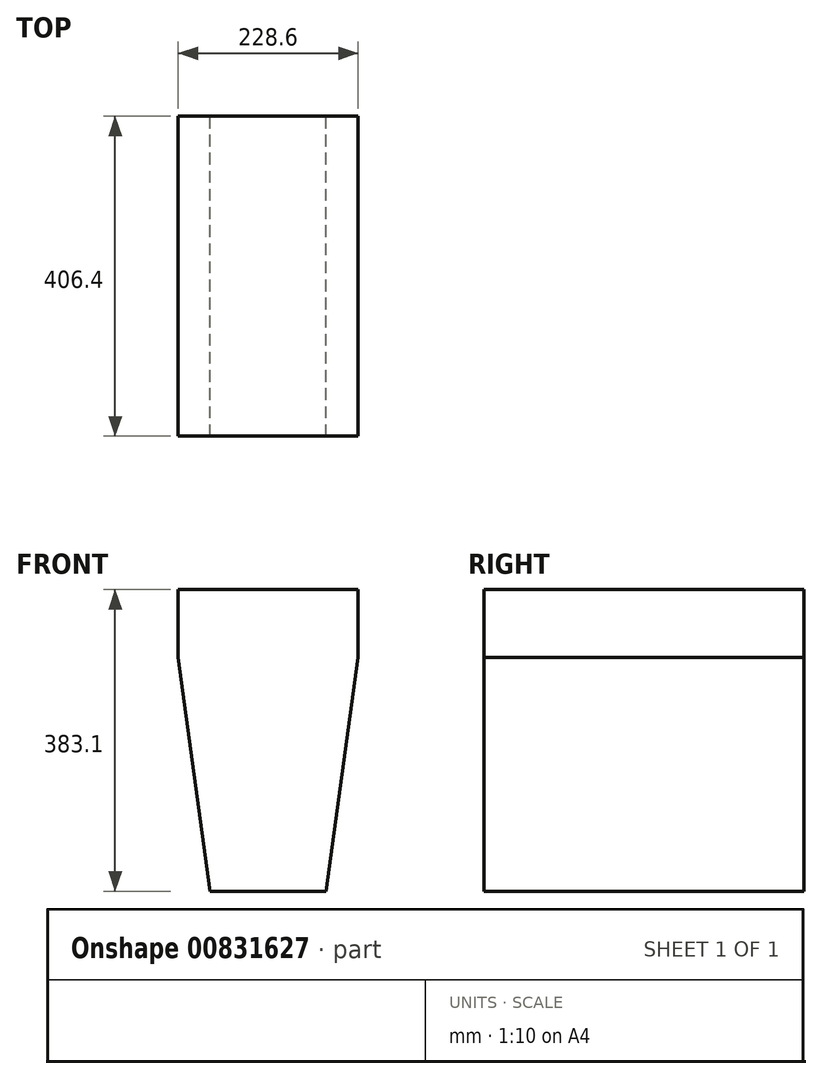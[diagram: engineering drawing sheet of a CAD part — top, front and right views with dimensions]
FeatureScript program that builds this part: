
annotation { "Feature Type Name" : "Feature", "Feature Type Description" : "" }
export const myFeature = defineFeature(function(context is Context, id is Id, definition is map)
    precondition{}
    {
        {
            var Q0;
            Q0=qCreatedBy(makeId("Front.planeOp"),FACE);
            var sketch = newSketch(context, id + "F0", { "sketchPlane" : qUnion([Q0])});
            skLineSegment(sketch, "E0", {"start": v(-115.25, 172.4) * mm, "end": v(113.35, 172.4) * mm});
            skLineSegment(sketch, "E1", {"start": v(113.35, 172.4) * mm, "end": v(113.35, 86.1) * mm});
            skLineSegment(sketch, "E2", {"start": v(113.35, 86.1) * mm, "end": v(72.7, -210.69) * mm});
            skLineSegment(sketch, "E3", {"start": v(72.7, -210.69) * mm, "end": v(-74.61, -210.69) * mm});
            skLineSegment(sketch, "E4", {"start": v(-74.61, -210.69) * mm, "end": v(-115.25, 86.1) * mm});
            skLineSegment(sketch, "E5", {"start": v(-115.25, 86.1) * mm, "end": v(-115.25, 172.4) * mm});
            skSolve(sketch);
        }
        {
            var Q0;
            Q0 = qSketchRegion(id + "F0", true);
            extrude(context, id + "F1", {"entities" : qUnion([Q0]), "depth" : 406.4 * mm, "offsetDistance" : 25.4 * mm});
        }
    });
